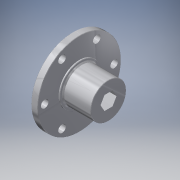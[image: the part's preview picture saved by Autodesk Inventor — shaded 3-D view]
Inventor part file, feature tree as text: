
AUTODESK INVENTOR PART (.ipt)
format: ipt  version: 2016 (Build 200138000, 138)  size: 163,328 bytes
history: native  units: in
note: dims shown in document units (in); Inventor stores cm internally (conversion verified against a paired STEP export)
features: chamfer x1
ambient origin geometry x8: Origin, YZ Plane, XZ Plane, XY Plane, X Axis, Y Axis, Z Axis, Center Point
bodies: Solid1 (feature_tree)
feature tree (1):
  chamfer  "Chamfer4"  [1 undecoded]
note: 1 required parameter value undecoded (feature->parameter linkage not recoverable at this tier; creation-order binding heuristic only, values carry confidence <= 0.55)
